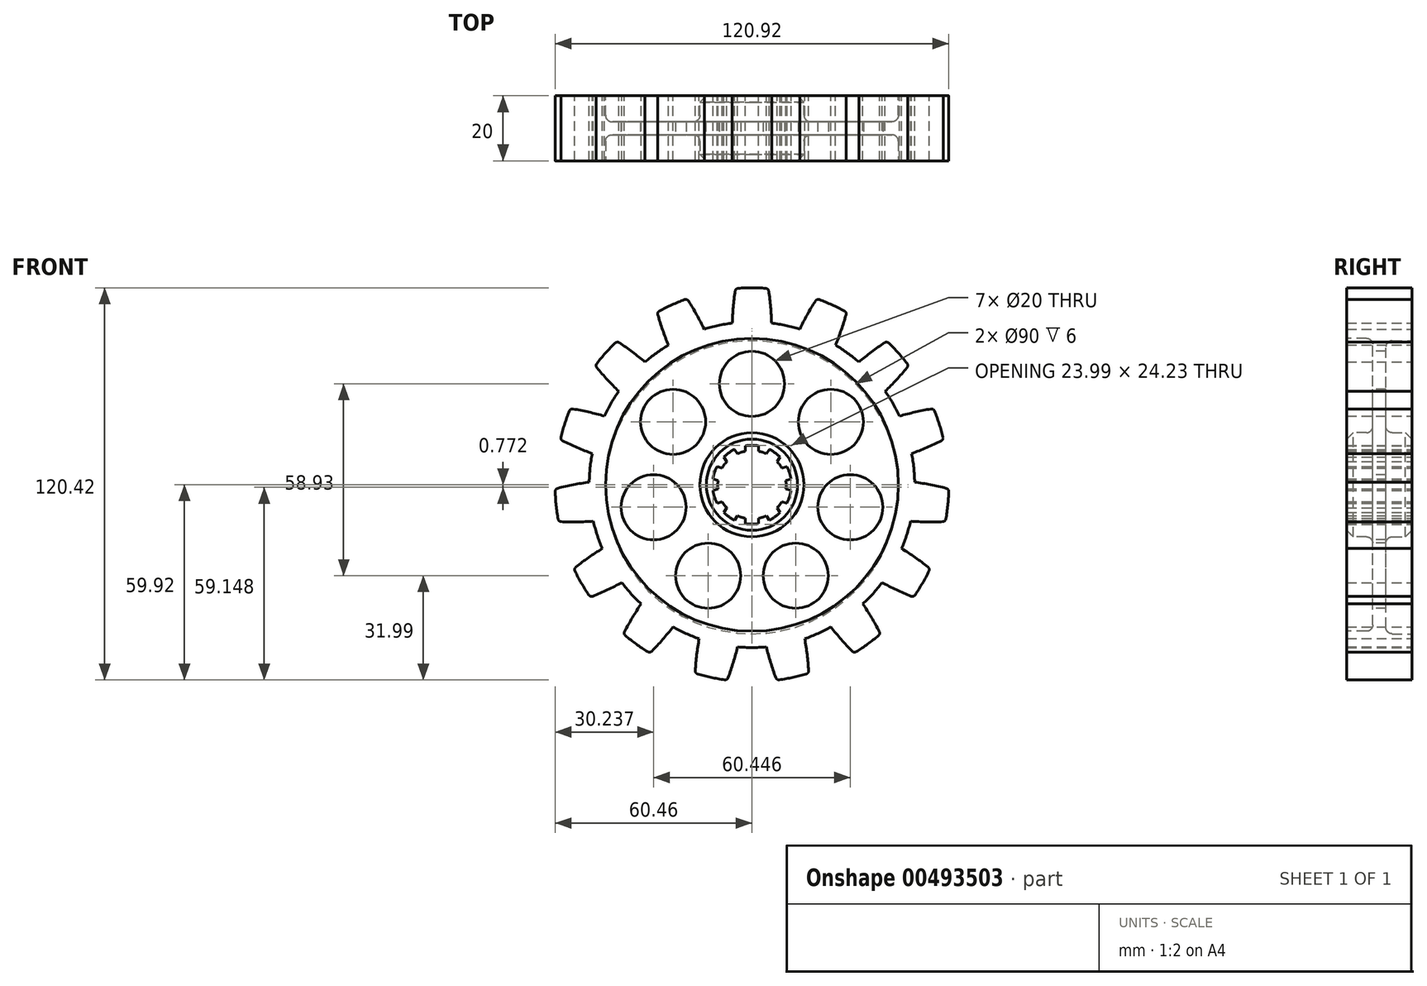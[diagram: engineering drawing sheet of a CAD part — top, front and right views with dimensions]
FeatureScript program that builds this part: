
annotation { "Feature Type Name" : "Feature", "Feature Type Description" : "" }
export const myFeature = defineFeature(function(context is Context, id is Id, definition is map)
    precondition{}
    {
        {
            var Q0;
            Q0=qCreatedBy(makeId("Front.planeOp"),FACE);
            var sketch = newSketch(context, id + "F0", { "sketchPlane" : qUnion([Q0])});
            skCircle(sketch, "E0", {"center": v(0, 0) * mm, "radius": 50 * mm});
            skCircle(sketch, "E1", {"center": v(0, 0) * mm, "radius": 10.5 * mm});
            skArc(sketch, "E2", {"start": v(2.05, 11.95) * mm, "mid": v(0, 12.12) * mm, "end": v(-2.05, 11.95) * mm});
            skLineSegment(sketch, "E3", {"start": v(-2.05, 11.95) * mm, "end": v(-2.05, 10.3) * mm});
            skLineSegment(sketch, "E4", {"start": v(2.05, 10.3) * mm, "end": v(2.05, 11.95) * mm});
            skArc(sketch, "E5", {"start": v(5.04, 60.29) * mm, "mid": v(0, 60.5) * mm, "end": v(-5.04, 60.29) * mm});
            skLineSegment(sketch, "E6", {"start": v(0, 50) * mm, "end": v(0, 46.5) * mm, "construction": true});
            skLineSegment(sketch, "E7", {"start": v(0, 46.5) * mm, "end": v(83.9, 46.5) * mm, "construction": true});
            skArc(sketch, "E8", {"start": v(-5.04, 60.29) * mm, "mid": v(-5.7, 54.98) * mm, "end": v(-6.05, 49.63) * mm});
            skArc(sketch, "E9.MirrorCS", {"start": v(5.04, 60.29) * mm, "mid": v(5.7, 54.98) * mm, "end": v(6.05, 49.63) * mm});
            skLineSegment(sketch, "E10.1.0", {"start": v(-4.4, 9.54) * mm, "end": v(-5.36, 10.87) * mm});
            skLineSegment(sketch, "E10.1.1", {"start": v(-8.68, 8.46) * mm, "end": v(-7.71, 7.13) * mm});
            skArc(sketch, "E10.1.2", {"start": v(-5.36, 10.87) * mm, "mid": v(-7.12, 9.8) * mm, "end": v(-8.68, 8.46) * mm});
            skLineSegment(sketch, "E10.2.0", {"start": v(-9.16, 5.13) * mm, "end": v(-10.73, 5.64) * mm});
            skLineSegment(sketch, "E10.2.1", {"start": v(-12, 1.74) * mm, "end": v(-10.43, 1.23) * mm});
            skArc(sketch, "E10.2.2", {"start": v(-10.73, 5.64) * mm, "mid": v(-11.52, 3.74) * mm, "end": v(-12, 1.74) * mm});
            skLineSegment(sketch, "E10.3.0", {"start": v(-10.43, -1.23) * mm, "end": v(-12, -1.74) * mm});
            skLineSegment(sketch, "E10.3.1", {"start": v(-10.73, -5.64) * mm, "end": v(-9.16, -5.13) * mm});
            skArc(sketch, "E10.3.2", {"start": v(-12, -1.74) * mm, "mid": v(-11.52, -3.74) * mm, "end": v(-10.73, -5.64) * mm});
            skLineSegment(sketch, "E10.4.0", {"start": v(-7.71, -7.13) * mm, "end": v(-8.68, -8.46) * mm});
            skLineSegment(sketch, "E10.4.1", {"start": v(-5.36, -10.87) * mm, "end": v(-4.4, -9.54) * mm});
            skArc(sketch, "E10.4.2", {"start": v(-8.68, -8.46) * mm, "mid": v(-7.12, -9.8) * mm, "end": v(-5.36, -10.87) * mm});
            skLineSegment(sketch, "E10.5.0", {"start": v(-2.05, -10.3) * mm, "end": v(-2.05, -11.95) * mm});
            skLineSegment(sketch, "E10.5.1", {"start": v(2.05, -11.95) * mm, "end": v(2.05, -10.3) * mm});
            skArc(sketch, "E10.5.2", {"start": v(-2.05, -11.95) * mm, "mid": v(0, -12.12) * mm, "end": v(2.05, -11.95) * mm});
            skLineSegment(sketch, "E10.6.0", {"start": v(4.4, -9.54) * mm, "end": v(5.36, -10.87) * mm});
            skLineSegment(sketch, "E10.6.1", {"start": v(8.68, -8.46) * mm, "end": v(7.71, -7.13) * mm});
            skArc(sketch, "E10.6.2", {"start": v(5.36, -10.87) * mm, "mid": v(7.12, -9.8) * mm, "end": v(8.68, -8.46) * mm});
            skLineSegment(sketch, "E10.7.0", {"start": v(9.16, -5.13) * mm, "end": v(10.73, -5.64) * mm});
            skLineSegment(sketch, "E10.7.1", {"start": v(12, -1.74) * mm, "end": v(10.43, -1.23) * mm});
            skArc(sketch, "E10.7.2", {"start": v(10.73, -5.64) * mm, "mid": v(11.52, -3.74) * mm, "end": v(12, -1.74) * mm});
            skLineSegment(sketch, "E10.8.0", {"start": v(10.43, 1.23) * mm, "end": v(12, 1.74) * mm});
            skLineSegment(sketch, "E10.8.1", {"start": v(10.73, 5.64) * mm, "end": v(9.16, 5.13) * mm});
            skArc(sketch, "E10.8.2", {"start": v(12, 1.74) * mm, "mid": v(11.52, 3.74) * mm, "end": v(10.73, 5.64) * mm});
            skLineSegment(sketch, "E10.9.0", {"start": v(7.71, 7.13) * mm, "end": v(8.68, 8.46) * mm});
            skLineSegment(sketch, "E10.9.1", {"start": v(5.36, 10.87) * mm, "end": v(4.4, 9.54) * mm});
            skArc(sketch, "E10.9.2", {"start": v(8.68, 8.46) * mm, "mid": v(7.12, 9.8) * mm, "end": v(5.36, 10.87) * mm});
            skSolve(sketch);
        }
        {
            var Q0;
            Q0=makeQuery(id+"F0.imprint","IMPRINT",FACE,{"disambiguationData":[TD([[makeQuery(id+"F0.imprint","IMPRINT",EDGE,{"derivedFrom":sQuery(id+"F0.wireOp",EDGE,"E5")}),1.0]])]});
            extrude(context, id + "F1", {"entities" : qUnion([Q0]), "depth" : 20 * mm});
        }
        {
            var Q0;
            Q0=makeQuery(id+"F0.imprint","IMPRINT",FACE,{"disambiguationData":[TD([[makeQuery(id+"F0.imprint","IMPRINT",EDGE,{"derivedFrom":sQuery(id+"F0.wireOp",EDGE,"E2")}),-1.0]])]});
            extrude(context, id + "F2", {"entities" : qUnion([Q0]), "depth" : 20 * mm});
        }
        {
            var Q0;
            Q0=makeQuery(id+"F1.opExtrude","SWEPT_EDGE",EDGE,{"disambiguationData":[OSD([sQuery(id+"F0.wireOp",EDGE,"E5"),sQuery(id+"F0.wireOp",EDGE,"E8")])]});
            var Q1;
            Q1=makeQuery(id+"F1.opExtrude","SWEPT_EDGE",EDGE,{"disambiguationData":[OSD([sQuery(id+"F0.wireOp",EDGE,"E5"),sQuery(id+"F0.wireOp",EDGE,"E9.MirrorCS")])]});
            fillet(context, id + "F3", {"entities" : qUnion([Q0, Q1]), "radius" : 1 * mm, "tangentPropagation" : true, "allowEdgeOverflow" : false});
        }
        {
            var Q0;
            Q0=makeQuery(id+"F1.opExtrude","SWEPT_BODY",BODY,{"disambiguationData":[OSD([sQuery(id+"F0.wireOp",EDGE,"E0"),sQuery(id+"F0.wireOp",EDGE,"E5"),sQuery(id+"F0.wireOp",EDGE,"E8"),sQuery(id+"F0.wireOp",EDGE,"E9.MirrorCS")])]});
            var Q1;
            Q1=sQuery(id+"F0.wireOp",EDGE,"E0");
            circularPattern(context, id + "F4", {"operationType" : NewBodyOperationType.ADD, "entities" : qUnion([Q0]), "axis" : qUnion([Q1]), "angle" : 360 * degree, "instanceCount" : 15, "equalSpace" : true});
        }
        {
            var Q0;
            Q0=makeQuery(id+"F2.opExtrude","CAP_FACE",FACE,{"disambiguationData":[OSD([sQuery(id+"F0.wireOp",EDGE,"E0"),sQuery(id+"F0.wireOp",EDGE,"E1"),sQuery(id+"F0.wireOp",EDGE,"E2"),sQuery(id+"F0.wireOp",EDGE,"E3"),sQuery(id+"F0.wireOp",EDGE,"E4"),sQuery(id+"F0.wireOp",EDGE,"E10.1.0"),sQuery(id+"F0.wireOp",EDGE,"E10.1.1"),sQuery(id+"F0.wireOp",EDGE,"E10.1.2"),sQuery(id+"F0.wireOp",EDGE,"E10.2.0"),sQuery(id+"F0.wireOp",EDGE,"E10.2.1"),sQuery(id+"F0.wireOp",EDGE,"E10.2.2"),sQuery(id+"F0.wireOp",EDGE,"E10.3.0"),sQuery(id+"F0.wireOp",EDGE,"E10.3.1"),sQuery(id+"F0.wireOp",EDGE,"E10.3.2"),sQuery(id+"F0.wireOp",EDGE,"E10.4.0"),sQuery(id+"F0.wireOp",EDGE,"E10.4.1"),sQuery(id+"F0.wireOp",EDGE,"E10.4.2"),sQuery(id+"F0.wireOp",EDGE,"E10.5.0"),sQuery(id+"F0.wireOp",EDGE,"E10.5.1"),sQuery(id+"F0.wireOp",EDGE,"E10.5.2"),sQuery(id+"F0.wireOp",EDGE,"E10.6.0"),sQuery(id+"F0.wireOp",EDGE,"E10.6.1"),sQuery(id+"F0.wireOp",EDGE,"E10.6.2"),sQuery(id+"F0.wireOp",EDGE,"E10.7.0"),sQuery(id+"F0.wireOp",EDGE,"E10.7.1"),sQuery(id+"F0.wireOp",EDGE,"E10.7.2"),sQuery(id+"F0.wireOp",EDGE,"E10.8.0"),sQuery(id+"F0.wireOp",EDGE,"E10.8.1"),sQuery(id+"F0.wireOp",EDGE,"E10.8.2"),sQuery(id+"F0.wireOp",EDGE,"E10.9.0"),sQuery(id+"F0.wireOp",EDGE,"E10.9.1"),sQuery(id+"F0.wireOp",EDGE,"E10.9.2")])],"isStart":false});
            var sketch = newSketch(context, id + "F5", { "sketchPlane" : qUnion([Q0])});
            skLineSegment(sketch, "E11", {"start": v(0, 0) * mm, "end": v(0, 31) * mm, "construction": true});
            skCircle(sketch, "E12", {"center": v(0, 31) * mm, "radius": 10 * mm});
            skCircle(sketch, "E13.1.0", {"center": v(-24.24, 19.33) * mm, "radius": 10 * mm});
            skCircle(sketch, "E13.2.0", {"center": v(-30.22, -6.9) * mm, "radius": 10 * mm});
            skCircle(sketch, "E13.3.0", {"center": v(-13.45, -27.93) * mm, "radius": 10 * mm});
            skCircle(sketch, "E13.4.0", {"center": v(13.45, -27.93) * mm, "radius": 10 * mm});
            skCircle(sketch, "E13.5.0", {"center": v(30.22, -6.9) * mm, "radius": 10 * mm});
            skCircle(sketch, "E13.6.0", {"center": v(24.24, 19.33) * mm, "radius": 10 * mm});
            skPoint(sketch, "E13.center", {"position": v(0, 0) * mm});
            skSolve(sketch);
        }
        {
            var Q0;
            Q0=makeQuery(id+"F5.imprint","IMPRINT",FACE,{"disambiguationData":[TD([[makeQuery(id+"F5.imprint","IMPRINT",EDGE,{"derivedFrom":sQuery(id+"F5.wireOp",EDGE,"E12")}),1.0]])]});
            var Q1;
            Q1=makeQuery(id+"F5.imprint","IMPRINT",FACE,{"disambiguationData":[TD([[makeQuery(id+"F5.imprint","IMPRINT",EDGE,{"derivedFrom":sQuery(id+"F5.wireOp",EDGE,"E13.6.0")}),1.0]])]});
            var Q2;
            Q2=makeQuery(id+"F5.imprint","IMPRINT",FACE,{"disambiguationData":[TD([[makeQuery(id+"F5.imprint","IMPRINT",EDGE,{"derivedFrom":sQuery(id+"F5.wireOp",EDGE,"E13.5.0")}),1.0]])]});
            var Q3;
            Q3=makeQuery(id+"F5.imprint","IMPRINT",FACE,{"disambiguationData":[TD([[makeQuery(id+"F5.imprint","IMPRINT",EDGE,{"derivedFrom":sQuery(id+"F5.wireOp",EDGE,"E13.4.0")}),1.0]])]});
            var Q4;
            Q4=makeQuery(id+"F5.imprint","IMPRINT",FACE,{"disambiguationData":[TD([[makeQuery(id+"F5.imprint","IMPRINT",EDGE,{"derivedFrom":sQuery(id+"F5.wireOp",EDGE,"E13.3.0")}),1.0]])]});
            var Q5;
            Q5=makeQuery(id+"F5.imprint","IMPRINT",FACE,{"disambiguationData":[TD([[makeQuery(id+"F5.imprint","IMPRINT",EDGE,{"derivedFrom":sQuery(id+"F5.wireOp",EDGE,"E13.2.0")}),1.0]])]});
            var Q6;
            Q6=makeQuery(id+"F5.imprint","IMPRINT",FACE,{"disambiguationData":[TD([[makeQuery(id+"F5.imprint","IMPRINT",EDGE,{"derivedFrom":sQuery(id+"F5.wireOp",EDGE,"E13.1.0")}),1.0]])]});
            extrude(context, id + "F6", {"entities" : qUnion([Q0, Q1, Q2, Q3, Q4, Q5, Q6]), "operationType" : NewBodyOperationType.REMOVE, "oppositeDirection" : true, "depth" : 25 * mm, "offsetDistance" : 25 * mm});
        }
        {
            var Q0;
            Q0=makeQuery(id+"F2.opExtrude","CAP_FACE",FACE,{"disambiguationData":[OSD([sQuery(id+"F0.wireOp",EDGE,"E0"),sQuery(id+"F0.wireOp",EDGE,"E1"),sQuery(id+"F0.wireOp",EDGE,"E2"),sQuery(id+"F0.wireOp",EDGE,"E3"),sQuery(id+"F0.wireOp",EDGE,"E4"),sQuery(id+"F0.wireOp",EDGE,"E10.1.0"),sQuery(id+"F0.wireOp",EDGE,"E10.1.1"),sQuery(id+"F0.wireOp",EDGE,"E10.1.2"),sQuery(id+"F0.wireOp",EDGE,"E10.2.0"),sQuery(id+"F0.wireOp",EDGE,"E10.2.1"),sQuery(id+"F0.wireOp",EDGE,"E10.2.2"),sQuery(id+"F0.wireOp",EDGE,"E10.3.0"),sQuery(id+"F0.wireOp",EDGE,"E10.3.1"),sQuery(id+"F0.wireOp",EDGE,"E10.3.2"),sQuery(id+"F0.wireOp",EDGE,"E10.4.0"),sQuery(id+"F0.wireOp",EDGE,"E10.4.1"),sQuery(id+"F0.wireOp",EDGE,"E10.4.2"),sQuery(id+"F0.wireOp",EDGE,"E10.5.0"),sQuery(id+"F0.wireOp",EDGE,"E10.5.1"),sQuery(id+"F0.wireOp",EDGE,"E10.5.2"),sQuery(id+"F0.wireOp",EDGE,"E10.6.0"),sQuery(id+"F0.wireOp",EDGE,"E10.6.1"),sQuery(id+"F0.wireOp",EDGE,"E10.6.2"),sQuery(id+"F0.wireOp",EDGE,"E10.7.0"),sQuery(id+"F0.wireOp",EDGE,"E10.7.1"),sQuery(id+"F0.wireOp",EDGE,"E10.7.2"),sQuery(id+"F0.wireOp",EDGE,"E10.8.0"),sQuery(id+"F0.wireOp",EDGE,"E10.8.1"),sQuery(id+"F0.wireOp",EDGE,"E10.8.2"),sQuery(id+"F0.wireOp",EDGE,"E10.9.0"),sQuery(id+"F0.wireOp",EDGE,"E10.9.1"),sQuery(id+"F0.wireOp",EDGE,"E10.9.2")])],"isStart":false});
            var sketch = newSketch(context, id + "F7", { "sketchPlane" : qUnion([Q0])});
            skCircle(sketch, "E14", {"center": v(0, 0) * mm, "radius": 45 * mm});
            skCircle(sketch, "E15", {"center": v(0, 0) * mm, "radius": 16 * mm});
            skSolve(sketch);
        }
        {
            var Q0;
            Q0=makeQuery(id+"F7.imprint","IMPRINT",FACE,{"disambiguationData":[TD([[makeQuery(id+"F7.imprint","IMPRINT",EDGE,{"derivedFrom":sQuery(id+"F7.wireOp",EDGE,"E14")}),1.0]])]});
            extrude(context, id + "F8", {"entities" : qUnion([Q0]), "operationType" : NewBodyOperationType.REMOVE, "oppositeDirection" : true, "depth" : 8 * mm, "offsetDistance" : 25 * mm});
        }
        {
            var Q0;
            Q0=makeQuery(id+"F8.boolean.opBoolean","COPY",EDGE,{"derivedFrom":makeQuery(id+"F8.opExtrude","CAP_EDGE",EDGE,{"disambiguationData":[OSD([sQuery(id+"F7.wireOp",EDGE,"E15")])],"isStart":false})});
            var Q1;
            Q1=makeQuery(id+"F8.boolean.opBoolean","COPY",EDGE,{"derivedFrom":makeQuery(id+"F8.opExtrude","CAP_EDGE",EDGE,{"disambiguationData":[OSD([sQuery(id+"F7.wireOp",EDGE,"E14")])],"isStart":false})});
            fillet(context, id + "F9", {"entities" : qUnion([Q0, Q1]), "radius" : 2 * mm, "tangentPropagation" : true, "allowEdgeOverflow" : false});
        }
        {
            var Q0;
            Q0=makeQuery(id+"F8.boolean.opBoolean","COPY",EDGE,{"derivedFrom":makeQuery(id+"F8.opExtrude","CAP_EDGE",EDGE,{"disambiguationData":[OSD([sQuery(id+"F7.wireOp",EDGE,"E15")])],"isStart":true})});
            var Q1;
            Q1=makeQuery(id+"F8.boolean.opBoolean","COPY",EDGE,{"derivedFrom":makeQuery(id+"F8.opExtrude","CAP_EDGE",EDGE,{"disambiguationData":[OSD([sQuery(id+"F7.wireOp",EDGE,"E14")])],"isStart":true})});
            chamfer(context, id + "F10", {"entities" : qUnion([Q0, Q1]), "width" : 2 * mm, "tangentPropagation" : true});
        }
        {
            var Q0;
            Q0=makeQuery(id+"F0.imprint","IMPRINT",FACE,{"disambiguationData":[TD([[makeQuery(id+"F0.imprint","IMPRINT",EDGE,{"derivedFrom":sQuery(id+"F0.wireOp",EDGE,"E2")}),-1.0]])]});
            var sketch = newSketch(context, id + "F11", { "sketchPlane" : qUnion([Q0])});
            skCircle(sketch, "E16", {"center": v(0, 0) * mm, "radius": 16 * mm});
            skCircle(sketch, "E17", {"center": v(0, -0.77) * mm, "radius": 45 * mm});
            skSolve(sketch);
        }
        {
            var Q0;
            Q0=makeQuery(id+"F11.imprint","IMPRINT",FACE,{"disambiguationData":[TD([[makeQuery(id+"F11.imprint","IMPRINT",EDGE,{"derivedFrom":sQuery(id+"F11.wireOp",EDGE,"E16")}),-1.0]])]});
            extrude(context, id + "F12", {"entities" : qUnion([Q0]), "operationType" : NewBodyOperationType.REMOVE, "depth" : 8 * mm, "offsetDistance" : 25 * mm});
        }
        {
            var Q0;
            Q0=makeQuery(id+"F12.boolean.opBoolean","COPY",EDGE,{"derivedFrom":makeQuery(id+"F12.opExtrude","CAP_EDGE",EDGE,{"disambiguationData":[OSD([sQuery(id+"F11.wireOp",EDGE,"E17")])],"isStart":true})});
            var Q1;
            Q1=makeQuery(id+"F12.boolean.opBoolean","COPY",EDGE,{"derivedFrom":makeQuery(id+"F12.opExtrude","CAP_EDGE",EDGE,{"disambiguationData":[OSD([sQuery(id+"F11.wireOp",EDGE,"E16")])],"isStart":true})});
            chamfer(context, id + "F13", {"entities" : qUnion([Q0, Q1]), "width" : 2 * mm, "tangentPropagation" : true});
        }
        {
            var Q0;
            Q0=makeQuery(id+"F12.boolean.opBoolean","COPY",EDGE,{"derivedFrom":makeQuery(id+"F12.opExtrude","CAP_EDGE",EDGE,{"disambiguationData":[OSD([sQuery(id+"F11.wireOp",EDGE,"E17")])],"isStart":false})});
            var Q1;
            Q1=makeQuery(id+"F12.boolean.opBoolean","COPY",EDGE,{"derivedFrom":makeQuery(id+"F12.opExtrude","CAP_EDGE",EDGE,{"disambiguationData":[OSD([sQuery(id+"F11.wireOp",EDGE,"E16")])],"isStart":false})});
            fillet(context, id + "F14", {"entities" : qUnion([Q0, Q1]), "radius" : 2 * mm, "tangentPropagation" : true, "allowEdgeOverflow" : false});
        }
    });
